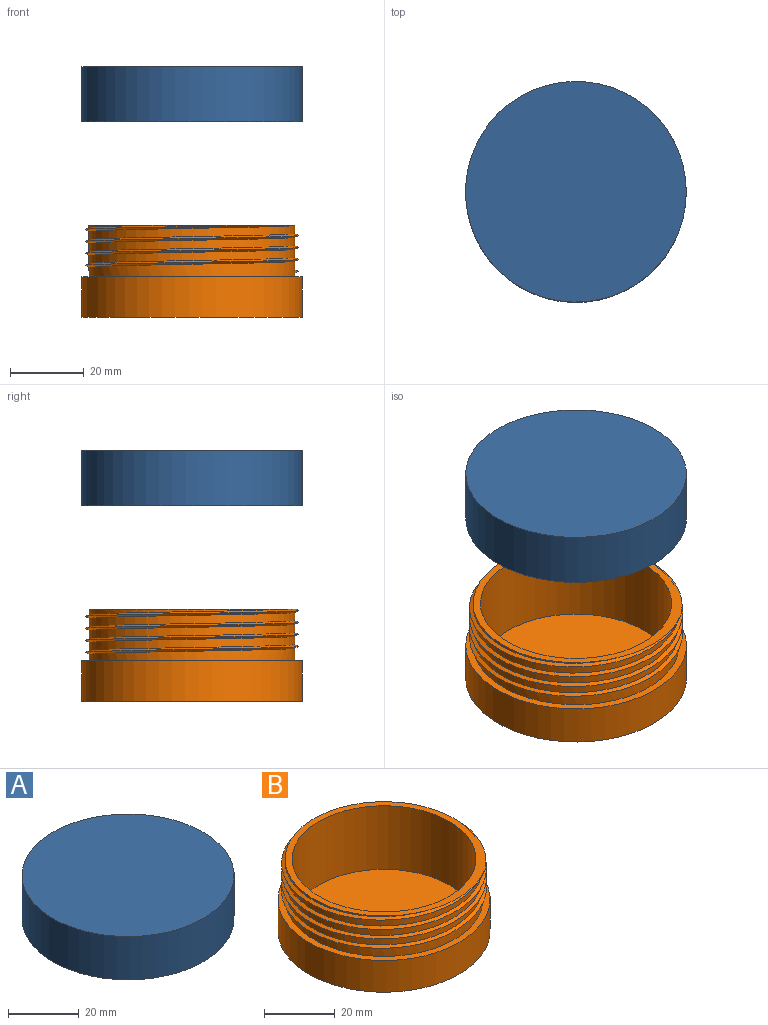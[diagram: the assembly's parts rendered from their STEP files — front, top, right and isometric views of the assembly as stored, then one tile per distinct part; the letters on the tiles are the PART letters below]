
ASSEMBLY  parts=2 mates=1
PART A: 7 faces, bbox 60x67x16 mm
  f0: cylinder r=30mm len=60mm, axis (0,0,1), area 2827.4mm2, adj f1,f2
  f1: plane 60x60mm, normal (0,0,1), area 2827.4mm2, adj f0
  f2: plane 60x60mm, normal (0,0,-1), area 337mm2, adj f0,f4,f5,f6
  f3: plane 56.4x56.02mm, normal (0,0,-1), area 2490.4mm2, adj f4,f5,f6
  f4: bspline ~66.97x58.01mm, area 739.8mm2, adj f2,f3,f5,f6
  f5: bspline ~66.97x58.01mm, area 739.3mm2, adj f2,f3,f4,f6
  f6: cylinder r=28mm len=56mm, axis (0,0,1), area 1450.2mm2, adj f2,f3,f4,f5
PART B: 14 faces, bbox 60.5x67.5x26.5 mm
  f0: bspline ~66.97x58.01mm, area 785.6mm2, adj f1,f2,f3,f4,f5,f7,f10
  f1: bspline ~66.97x58.01mm, area 754.4mm2, adj f0,f2,f3,f4,f5,f6,f7,f10
  f2: cylinder r=28mm len=56mm, axis (0,0,1), area 461.8mm2, adj f0,f1,f3,f10,f11
  f3: cylinder r=28mm len=56mm, axis (0,0,1), area 395.9mm2, adj f0,f1,f2,f4
  f4: cylinder r=28mm len=56mm, axis (0,0,1), area 395.9mm2, adj f0,f1,f3,f5
  f5: cylinder r=28mm len=56mm, axis (0,0,1), area 395.8mm2, adj f0,f1,f4,f6
  f6: cylinder r=28mm len=56mm, axis (0,0,1), area 137.3mm2, adj f1,f5,f7
  f7: plane 56.91x56.53mm, normal (0,0,1), area 366.7mm2, adj f0,f1,f6,f8
  f8: cylinder r=26mm len=52mm, axis (0,0,1), area 3594mm2, adj f7,f9
  f9: plane 52x52mm, normal (0,0,1), area 2123.7mm2, adj f8
  f10: plane 1x1mm, normal (0,-1,-0.02), area 0.5mm2, adj f0,f1,f2
  f11: plane 60x60mm, normal (0,0,1), area 364.4mm2, adj f2,f13
  f12: plane 60x60mm, normal (0,0,-1), area 2827.4mm2, adj f13
  f13: cylinder r=30mm len=60mm, axis (0,0,1), area 2073.5mm2, adj f11,f12
PLACE A rot(axis=(0,0,1),7.3deg) t=(0,0,40.14)mm
PLACE B at identity fixed
MATE cylindrical A.f0 <-> B.f2  axis (0,0,1) through (0,0,53.14)mm
